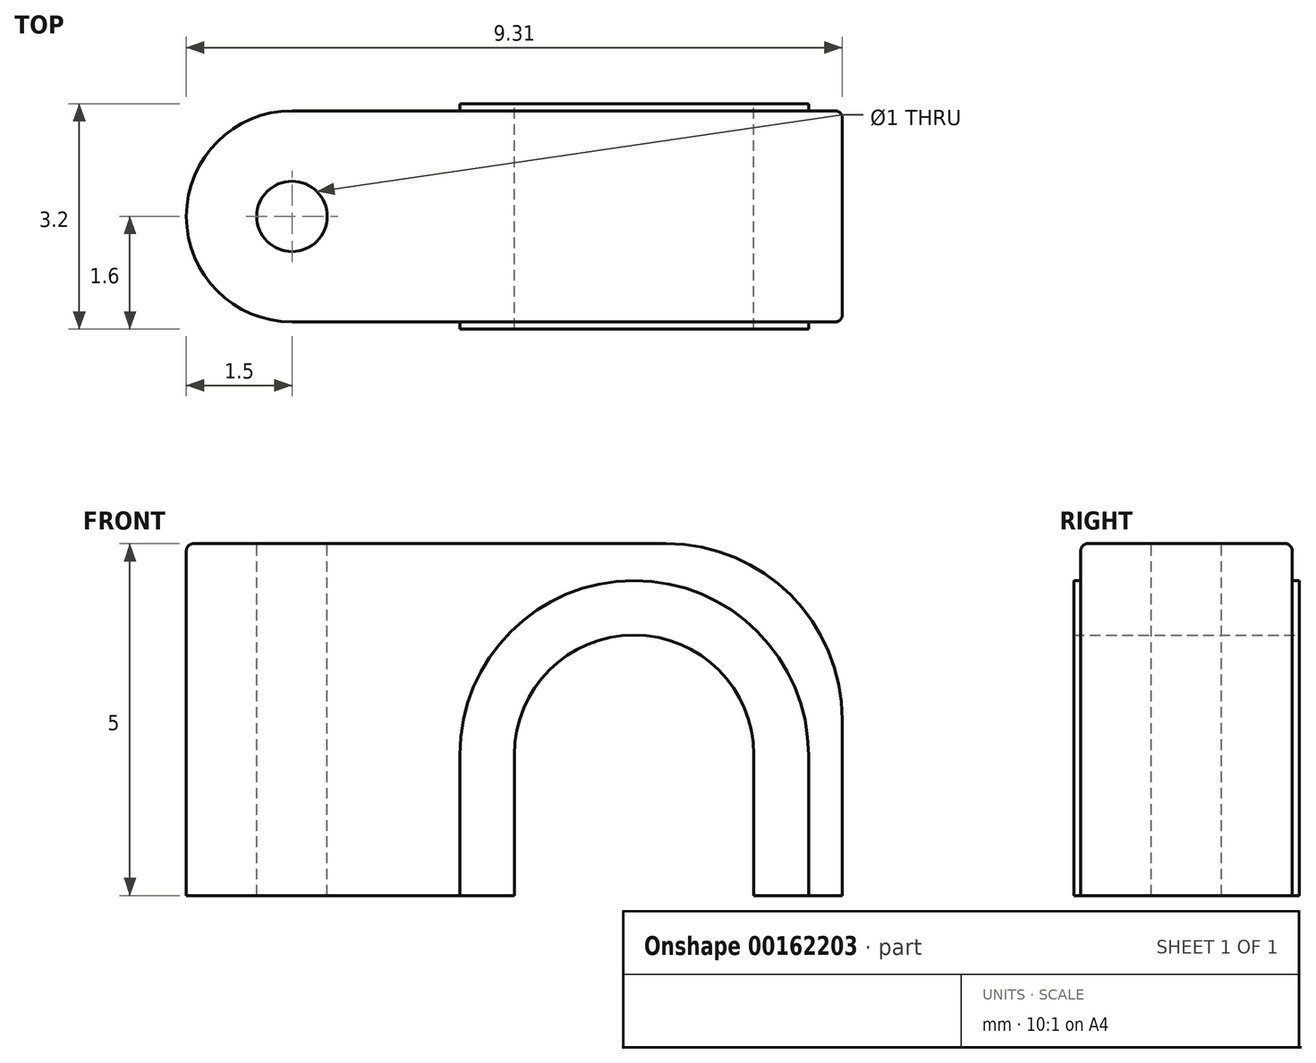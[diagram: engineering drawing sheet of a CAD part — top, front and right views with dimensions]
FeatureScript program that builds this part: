
annotation { "Feature Type Name" : "Feature", "Feature Type Description" : "" }
export const myFeature = defineFeature(function(context is Context, id is Id, definition is map)
    precondition{}
    {
        {
            var Q0;
            Q0=qCreatedBy(makeId("Front.planeOp"),FACE);
            var sketch = newSketch(context, id + "F0", { "sketchPlane" : qUnion([Q0])});
            skLineSegment(sketch, "E0.bottom", {"start": v(0, 0) * mm, "end": v(9.31, 0) * mm});
            skLineSegment(sketch, "E0.top", {"start": v(0, 5) * mm, "end": v(9.31, 5) * mm});
            skLineSegment(sketch, "E0.left", {"start": v(0, 0) * mm, "end": v(0, 5) * mm});
            skLineSegment(sketch, "E0.right", {"start": v(9.31, 0) * mm, "end": v(9.31, 5) * mm});
            skLineSegment(sketch, "E1", {"start": v(8.06, 0) * mm, "end": v(8.06, 2) * mm});
            skLineSegment(sketch, "E2", {"start": v(4.66, 0) * mm, "end": v(4.66, 2) * mm});
            skArc(sketch, "E3", {"start": v(8.06, 2) * mm, "mid": v(6.36, 3.7) * mm, "end": v(4.66, 2) * mm});
            skSolve(sketch);
        }
        {
            var Q0;
            Q0=makeQuery(id+"F0.imprint","IMPRINT",FACE,{"disambiguationData":[TD([[makeQuery(id+"F0.imprint","IMPRINT",EDGE,{"derivedFrom":sQuery(id+"F0.wireOp",EDGE,"E0.top")}),-1.0]])]});
            extrude(context, id + "F1", {"entities" : qUnion([Q0]), "depth" : 3 * mm});
        }
        {
            var Q0;
            Q0=makeQuery(id+"F1.opExtrude","CAP_EDGE",EDGE,{"disambiguationData":[OSD([sQuery(id+"F0.wireOp",EDGE,"E0.left")])],"isStart":true});
            var Q1;
            Q1=makeQuery(id+"F1.opExtrude","CAP_EDGE",EDGE,{"disambiguationData":[OSD([sQuery(id+"F0.wireOp",EDGE,"E0.left")])],"isStart":false});
            fillet(context, id + "F2", {"entities" : qUnion([Q0, Q1]), "radius" : 1.5 * mm, "tangentPropagation" : true, "allowEdgeOverflow" : false});
        }
        {
            var Q0;
            Q0=makeQuery(id+"F1.opExtrude","SWEPT_FACE",FACE,{"disambiguationData":[OSD([sQuery(id+"F0.wireOp",EDGE,"E0.top")])]});
            var sketch = newSketch(context, id + "F3", { "sketchPlane" : qUnion([Q0])});
            skLineSegment(sketch, "E4", {"start": v(1.5, 0) * mm, "end": v(1.5, -3) * mm, "construction": true});
            skPoint(sketch, "E5", {"position": v(1.5, -1.5) * mm});
            skSolve(sketch);
        }
        {
            var Q0;
            Q0=sQuery(id+"F3.wireOp",VERTEX,"E5");
            var Q1;
            Q1=makeQuery(id+"F1.opExtrude","SWEPT_BODY",BODY,{"disambiguationData":[OSD([sQuery(id+"F0.wireOp",EDGE,"E0.bottom"),sQuery(id+"F0.wireOp",EDGE,"E0.top"),sQuery(id+"F0.wireOp",EDGE,"E0.left"),sQuery(id+"F0.wireOp",EDGE,"E0.right"),sQuery(id+"F0.wireOp",EDGE,"E1"),sQuery(id+"F0.wireOp",EDGE,"E2"),sQuery(id+"F0.wireOp",EDGE,"E3")])]});
            hole(context, id + "F4", {"style" : HoleStyle.SIMPLE, "endStyle" : HoleEndStyle.THROUGH, "holeDiameter" : 1 * mm, "locations" : qUnion([Q0]), "scope" : qUnion([Q1]), "isTappedThrough" : true});
        }
        {
            var Q0;
            Q0=makeQuery(id+"F1.opExtrude","SWEPT_EDGE",EDGE,{"disambiguationData":[OSD([sQuery(id+"F0.wireOp",EDGE,"E0.top"),sQuery(id+"F0.wireOp",EDGE,"E0.right")])]});
            fillet(context, id + "F5", {"entities" : qUnion([Q0]), "radius" : 2.5 * mm, "tangentPropagation" : true, "allowEdgeOverflow" : false});
        }
        {
            var Q0;
            Q0=makeQuery(id+"F1.opExtrude","CAP_EDGE",EDGE,{"disambiguationData":[OSD([sQuery(id+"F0.wireOp",EDGE,"E0.top")])],"isStart":false});
            var Q1;
            {var subQ0=sQuery(id+"F0.wireOp",EDGE,"E0.right");var subQ1=sQuery(id+"F0.wireOp",EDGE,"E0.top");Q1=makeQuery(id+"F5.opFillet","BLEND_EDGE",EDGE,{"blendedFrom":[makeQuery(id+"F1.opExtrude","SWEPT_EDGE",EDGE,{"disambiguationData":[OSD([subQ1,subQ0])]}),makeQuery(id+"F1.opExtrude","CAP_FACE",FACE,{"disambiguationData":[OSD([sQuery(id+"F0.wireOp",EDGE,"E0.bottom"),subQ1,sQuery(id+"F0.wireOp",EDGE,"E0.left"),subQ0,sQuery(id+"F0.wireOp",EDGE,"E1"),sQuery(id+"F0.wireOp",EDGE,"E2"),sQuery(id+"F0.wireOp",EDGE,"E3")])],"isStart":false})],"blendedInto":[makeQuery(id+"F1.opExtrude","CAP_FACE",FACE,{"disambiguationData":[OSD([sQuery(id+"F0.wireOp",EDGE,"E0.bottom"),subQ1,sQuery(id+"F0.wireOp",EDGE,"E0.left"),subQ0,sQuery(id+"F0.wireOp",EDGE,"E1"),sQuery(id+"F0.wireOp",EDGE,"E2"),sQuery(id+"F0.wireOp",EDGE,"E3")])],"isStart":false})]});}
            var Q2;
            Q2=makeQuery(id+"F1.opExtrude","CAP_EDGE",EDGE,{"disambiguationData":[OSD([sQuery(id+"F0.wireOp",EDGE,"E0.right")])],"isStart":false});
            var Q3;
            Q3=makeQuery(id+"F1.opExtrude","CAP_EDGE",EDGE,{"disambiguationData":[OSD([sQuery(id+"F0.wireOp",EDGE,"E0.right")])],"isStart":true});
            var Q4;
            {var subQ0=sQuery(id+"F0.wireOp",EDGE,"E0.right");var subQ1=sQuery(id+"F0.wireOp",EDGE,"E0.top");Q4=makeQuery(id+"F5.opFillet","BLEND_EDGE",EDGE,{"blendedFrom":[makeQuery(id+"F1.opExtrude","SWEPT_EDGE",EDGE,{"disambiguationData":[OSD([subQ1,subQ0])]}),makeQuery(id+"F1.opExtrude","CAP_FACE",FACE,{"disambiguationData":[OSD([sQuery(id+"F0.wireOp",EDGE,"E0.bottom"),subQ1,sQuery(id+"F0.wireOp",EDGE,"E0.left"),subQ0,sQuery(id+"F0.wireOp",EDGE,"E1"),sQuery(id+"F0.wireOp",EDGE,"E2"),sQuery(id+"F0.wireOp",EDGE,"E3")])],"isStart":true})],"blendedInto":[makeQuery(id+"F1.opExtrude","CAP_FACE",FACE,{"disambiguationData":[OSD([sQuery(id+"F0.wireOp",EDGE,"E0.bottom"),subQ1,sQuery(id+"F0.wireOp",EDGE,"E0.left"),subQ0,sQuery(id+"F0.wireOp",EDGE,"E1"),sQuery(id+"F0.wireOp",EDGE,"E2"),sQuery(id+"F0.wireOp",EDGE,"E3")])],"isStart":true})]});}
            var Q5;
            Q5=makeQuery(id+"F1.opExtrude","CAP_EDGE",EDGE,{"disambiguationData":[OSD([sQuery(id+"F0.wireOp",EDGE,"E0.top")])],"isStart":true});
            fillet(context, id + "F6", {"entities" : qUnion([Q0, Q1, Q2, Q3, Q4, Q5]), "radius" : .1 * mm, "tangentPropagation" : true, "allowEdgeOverflow" : false});
        }
        {
            var Q0;
            Q0=makeQuery(id+"F1.opExtrude","CAP_FACE",FACE,{"disambiguationData":[OSD([sQuery(id+"F0.wireOp",EDGE,"E0.bottom"),sQuery(id+"F0.wireOp",EDGE,"E0.top"),sQuery(id+"F0.wireOp",EDGE,"E0.left"),sQuery(id+"F0.wireOp",EDGE,"E0.right"),sQuery(id+"F0.wireOp",EDGE,"E1"),sQuery(id+"F0.wireOp",EDGE,"E2"),sQuery(id+"F0.wireOp",EDGE,"E3")])],"isStart":false});
            var sketch = newSketch(context, id + "F7", { "sketchPlane" : qUnion([Q0])});
            skLineSegment(sketch, "E6.0", {"start": v(3.88, 0) * mm, "end": v(3.88, 2) * mm});
            skArc(sketch, "E6.1", {"start": v(8.83, 2) * mm, "mid": v(6.36, 4.48) * mm, "end": v(3.88, 2) * mm});
            skLineSegment(sketch, "E6.2", {"start": v(8.83, 0) * mm, "end": v(8.83, 2) * mm});
            skSolve(sketch);
        }
        {
            var Q0;
            {var subQ5=sQuery(id+"F7.wireOp",EDGE,"E6.0");Q0=makeQuery(id+"F7.imprint","IMPRINT",FACE,{"disambiguationData":[TD([[makeQuery(id+"F7.imprint","IMPRINT",EDGE,{"derivedFrom":subQ5}),-1.0]])]});}
            extrude(context, id + "F8", {"entities" : qUnion([Q0]), "operationType" : NewBodyOperationType.ADD, "depth" : .1 * mm, "hasSecondDirection" : true, "secondDirectionOppositeDirection" : true, "secondDirectionDepth" : 3.1 * mm});
        }
    });
